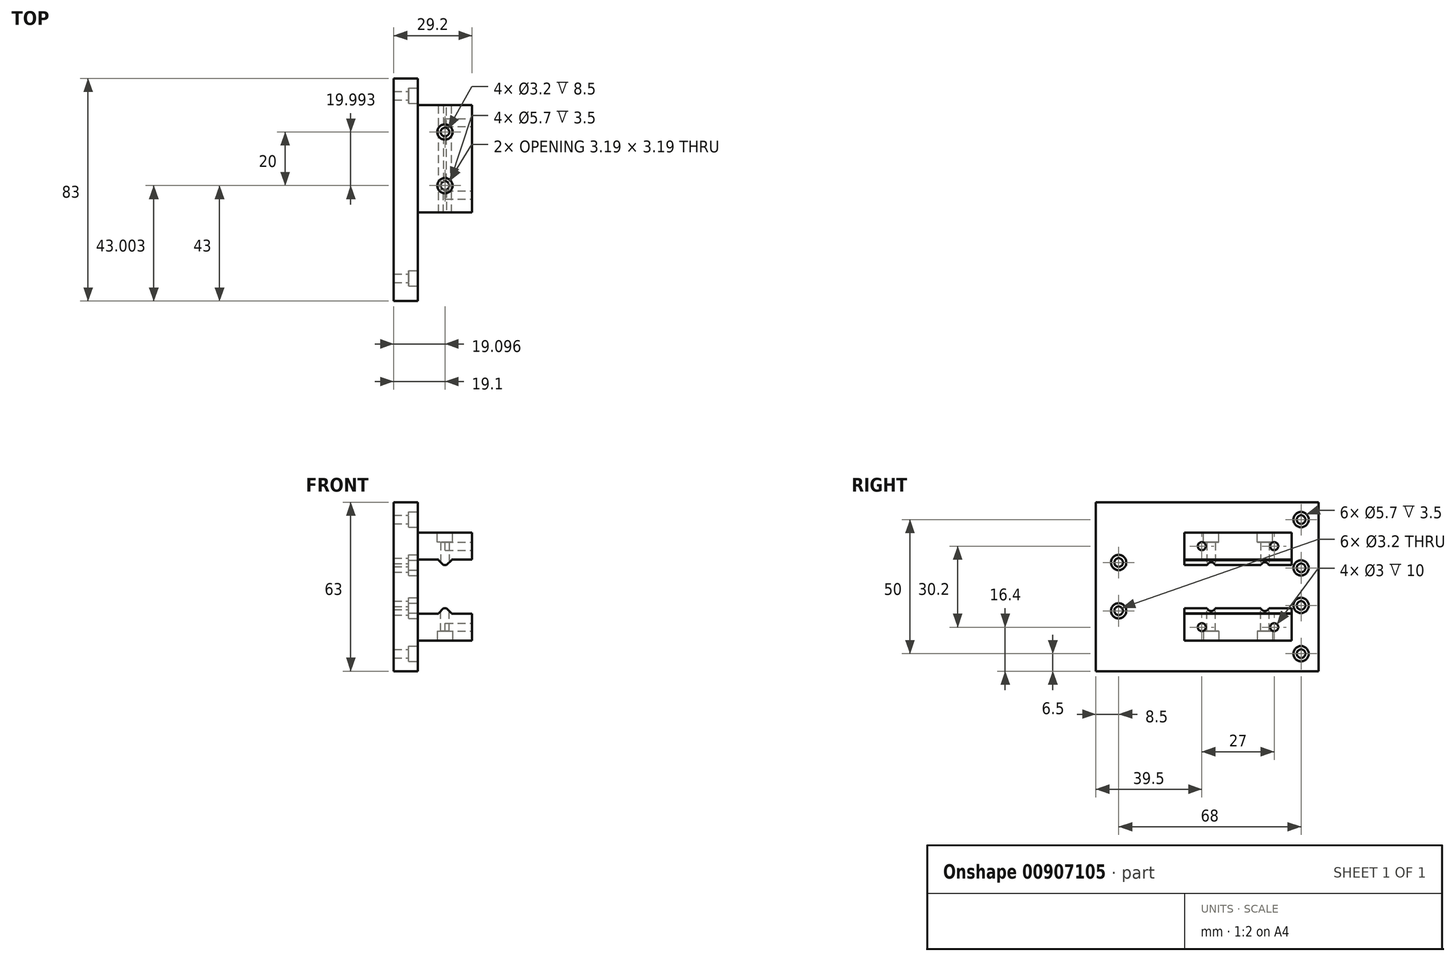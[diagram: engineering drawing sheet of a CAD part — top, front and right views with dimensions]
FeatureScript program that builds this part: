
annotation { "Feature Type Name" : "Feature", "Feature Type Description" : "" }
export const myFeature = defineFeature(function(context is Context, id is Id, definition is map)
    precondition{}
    {
        {
            assignVariable(context, id + "F0", {"name" : "headdepth", "anyValue" : 3.5 * mm});
        }
        {
            var Q0;
            Q0=qCreatedBy(makeId("Top.planeOp"),FACE);
            var sketch = newSketch(context, id + "F1", { "sketchPlane" : qUnion([Q0])});
            skLineSegment(sketch, "E0.bottom", {"start": v(0, 0) * mm, "end": v(9, 0) * mm});
            skLineSegment(sketch, "E0.top", {"start": v(0, 83) * mm, "end": v(9, 83) * mm});
            skLineSegment(sketch, "E0.left", {"start": v(0, 0) * mm, "end": v(0, 83) * mm});
            skLineSegment(sketch, "E0.right", {"start": v(9, 0) * mm, "end": v(9, 83) * mm});
            skSolve(sketch);
        }
        {
            var Q0;
            Q0=qSketchRegion(id+"F1",true);
            var Q1;
            Q1=makeQuery(id+"F1.imprint","IMPRINT",FACE,{"disambiguationData":[TD([[makeQuery(id+"F1.imprint","IMPRINT",EDGE,{"derivedFrom":sQuery(id+"F1.wireOp",EDGE,"E0.bottom")}),1.0]])]});
            extrude(context, id + "F2", {"entities" : qUnion([Q0, Q1]), "depth" : 63 * mm, "offsetDistance" : 25 * mm});
        }
        {
            var Q0;
            Q0=makeQuery(id+"F2.opExtrude","SWEPT_FACE",FACE,{"disambiguationData":[OSD([sQuery(id+"F1.wireOp",EDGE,"E0.right")])]});
            var sketch = newSketch(context, id + "F3", { "sketchPlane" : qUnion([Q0])});
            skLineSegment(sketch, "E1", {"start": v(83, 6.5) * mm, "end": v(0, 6.5) * mm, "construction": true});
            skLineSegment(sketch, "E2", {"start": v(0, 24.5) * mm, "end": v(83, 24.5) * mm, "construction": true});
            skLineSegment(sketch, "E3", {"start": v(83, 38.5) * mm, "end": v(0, 38.5) * mm, "construction": true});
            skLineSegment(sketch, "E4", {"start": v(0, 56.5) * mm, "end": v(83, 56.5) * mm, "construction": true});
            skLineSegment(sketch, "E5", {"start": v(76.5, 63) * mm, "end": v(76.5, 0) * mm, "construction": true});
            skLineSegment(sketch, "E6", {"start": v(8.5, 63) * mm, "end": v(8.5, 0) * mm, "construction": true});
            skLineSegment(sketch, "E7", {"start": v(0, 22.5) * mm, "end": v(8.5, 22.5) * mm, "construction": true});
            skLineSegment(sketch, "E8", {"start": v(0, 40.5) * mm, "end": v(8.5, 40.5) * mm, "construction": true});
            skCircle(sketch, "E9", {"center": v(8.5, 40.5) * mm, "radius": 2.85 * mm});
            skCircle(sketch, "E10", {"center": v(8.5, 22.5) * mm, "radius": 2.85 * mm});
            skCircle(sketch, "E11", {"center": v(76.5, 56.5) * mm, "radius": 2.85 * mm});
            skCircle(sketch, "E12", {"center": v(76.5, 38.5) * mm, "radius": 2.85 * mm});
            skCircle(sketch, "E13", {"center": v(76.5, 24.5) * mm, "radius": 2.85 * mm});
            skCircle(sketch, "E14", {"center": v(76.5, 6.5) * mm, "radius": 2.85 * mm});
            skSolve(sketch);
        }
        {
            var Q0;
            Q0=qSketchRegion(id+"F3",true);
            var Q1;
            Q1=makeQuery(id+"F3.imprint","IMPRINT",FACE,{"disambiguationData":[TD([[makeQuery(id+"F3.imprint","IMPRINT",EDGE,{"derivedFrom":sQuery(id+"F3.wireOp",EDGE,"E9")}),1.0]])]});
            extrude(context, id + "F4", {"entities" : qUnion([Q0, Q1]), "operationType" : NewBodyOperationType.REMOVE, "oppositeDirection" : true, "depth" : getVariable(context, 'headdepth'), "offsetDistance" : 25 * mm});
        }
        {
            var Q0;
            Q0=makeQuery(id+"F3.imprint","IMPRINT",FACE,{"disambiguationData":[TD([[makeQuery(id+"F3.imprint","IMPRINT",EDGE,{"derivedFrom":sQuery(id+"F3.wireOp",EDGE,"E9")}),1.0]])]});
            var sketch = newSketch(context, id + "F5", { "sketchPlane" : qUnion([Q0])});
            skCircle(sketch, "E15", {"center": v(8.5, 40.5) * mm, "radius": 1.6 * mm});
            skCircle(sketch, "E16", {"center": v(8.5, 22.5) * mm, "radius": 1.6 * mm});
            skCircle(sketch, "E17", {"center": v(76.5, 24.5) * mm, "radius": 1.6 * mm});
            skCircle(sketch, "E18", {"center": v(76.5, 38.5) * mm, "radius": 1.6 * mm});
            skCircle(sketch, "E19", {"center": v(76.5, 56.5) * mm, "radius": 1.6 * mm});
            skCircle(sketch, "E20", {"center": v(76.5, 6.5) * mm, "radius": 1.6 * mm});
            skSolve(sketch);
        }
        {
            var Q0;
            Q0=qSketchRegion(id+"F5",true);
            extrude(context, id + "F6", {"entities" : qUnion([Q0]), "operationType" : NewBodyOperationType.REMOVE, "oppositeDirection" : true, "depth" : 25 * mm, "offsetDistance" : 25 * mm});
        }
        {
            var Q0;
            Q0=makeQuery(id+"F2.opExtrude","SWEPT_FACE",FACE,{"disambiguationData":[OSD([sQuery(id+"F1.wireOp",EDGE,"E0.right")])]});
            var sketch = newSketch(context, id + "F7", { "sketchPlane" : qUnion([Q0])});
            skLineSegment(sketch, "E21", {"start": v(83, 31.5) * mm, "end": v(0, 31.5) * mm, "construction": true});
            skLineSegment(sketch, "E22.bottom", {"start": v(73, 41.6) * mm, "end": v(33, 41.6) * mm});
            skLineSegment(sketch, "E22.top", {"start": v(73, 51.6) * mm, "end": v(33, 51.6) * mm});
            skLineSegment(sketch, "E22.left", {"start": v(73, 41.6) * mm, "end": v(73, 51.6) * mm});
            skLineSegment(sketch, "E22.right", {"start": v(33, 41.6) * mm, "end": v(33, 51.6) * mm});
            skLineSegment(sketch, "E23.MirrorCS", {"start": v(73, 21.4) * mm, "end": v(73, 11.4) * mm});
            skLineSegment(sketch, "E24.MirrorCS", {"start": v(73, 21.4) * mm, "end": v(33, 21.4) * mm});
            skLineSegment(sketch, "E25.MirrorCS", {"start": v(73, 11.4) * mm, "end": v(33, 11.4) * mm});
            skLineSegment(sketch, "E26.MirrorCS", {"start": v(33, 21.4) * mm, "end": v(33, 11.4) * mm});
            skSolve(sketch);
        }
        {
            var Q0;
            Q0=makeQuery(id+"F7.imprint","IMPRINT",FACE,{"disambiguationData":[TD([[makeQuery(id+"F7.imprint","IMPRINT",EDGE,{"derivedFrom":sQuery(id+"F7.wireOp",EDGE,"E23.MirrorCS")}),-1.0]])]});
            var Q1;
            Q1=makeQuery(id+"F7.imprint","IMPRINT",FACE,{"disambiguationData":[TD([[makeQuery(id+"F7.imprint","IMPRINT",EDGE,{"derivedFrom":sQuery(id+"F7.wireOp",EDGE,"E22.bottom")}),-1.0]])]});
            extrude(context, id + "F8", {"entities" : qUnion([Q0, Q1]), "operationType" : NewBodyOperationType.ADD, "depth" : 20.2 * mm, "offsetDistance" : 25 * mm});
        }
        {
            var Q0;
            Q0=makeQuery(id+"F8.opExtrude","SWEPT_FACE",FACE,{"disambiguationData":[OSD([sQuery(id+"F7.wireOp",EDGE,"E22.bottom")])]});
            var sketch = newSketch(context, id + "F9", { "sketchPlane" : qUnion([Q0])});
            skLineSegment(sketch, "E27", {"start": v(19.1, -33) * mm, "end": v(19.1, -73) * mm, "construction": true});
            skLineSegment(sketch, "E28.bottom", {"start": v(21.5, -33) * mm, "end": v(16.7, -33) * mm});
            skLineSegment(sketch, "E28.top", {"start": v(21.5, -73) * mm, "end": v(16.7, -73) * mm});
            skLineSegment(sketch, "E28.left", {"start": v(21.5, -33) * mm, "end": v(21.5, -73) * mm});
            skLineSegment(sketch, "E28.right", {"start": v(16.7, -33) * mm, "end": v(16.7, -73) * mm});
            skSolve(sketch);
        }
        {
            var Q0;
            Q0=qSketchRegion(id+"F9",true);
            extrude(context, id + "F10", {"entities" : qUnion([Q0]), "operationType" : NewBodyOperationType.ADD, "depth" : 2 * mm, "offsetDistance" : 25 * mm});
        }
        {
            var Q0;
            Q0=makeQuery(id+"F10.opExtrude","CAP_EDGE",EDGE,{"disambiguationData":[OSD([sQuery(id+"F9.wireOp",EDGE,"E28.left")])],"isStart":false});
            var Q1;
            Q1=makeQuery(id+"F10.opExtrude","CAP_EDGE",EDGE,{"disambiguationData":[OSD([sQuery(id+"F9.wireOp",EDGE,"E28.right")])],"isStart":false});
            chamfer(context, id + "F11", {"entities" : qUnion([Q0, Q1]), "width" : 1.8 * mm, "tangentPropagation" : true});
        }
        {
            var Q0;
            Q0=makeQuery(id+"F10.opExtrude","CAP_FACE",FACE,{"disambiguationData":[OSD([sQuery(id+"F9.wireOp",EDGE,"E28.bottom"),sQuery(id+"F9.wireOp",EDGE,"E28.top"),sQuery(id+"F9.wireOp",EDGE,"E28.left"),sQuery(id+"F9.wireOp",EDGE,"E28.right")])],"isStart":false});
            var sketch = newSketch(context, id + "F12", { "sketchPlane" : qUnion([Q0])});
            skLineSegment(sketch, "E29", {"start": v(19.1, -33) * mm, "end": v(19.1, -73) * mm, "construction": true});
            skCircle(sketch, "E30", {"center": v(19.1, -43) * mm, "radius": 1.6 * mm});
            skCircle(sketch, "E31", {"center": v(19.1, -63) * mm, "radius": 1.6 * mm});
            skSolve(sketch);
        }
        {
            var Q0;
            Q0=qSketchRegion(id+"F12",true);
            extrude(context, id + "F13", {"entities" : qUnion([Q0]), "operationType" : NewBodyOperationType.REMOVE, "oppositeDirection" : true, "depth" : 25 * mm, "offsetDistance" : 25 * mm});
        }
        {
            var Q0;
            Q0=makeQuery(id+"F8.opExtrude","SWEPT_FACE",FACE,{"disambiguationData":[OSD([sQuery(id+"F7.wireOp",EDGE,"E24.MirrorCS")])]});
            var sketch = newSketch(context, id + "F14", { "sketchPlane" : qUnion([Q0])});
            skLineSegment(sketch, "E32", {"start": v(19.1, 73) * mm, "end": v(19.1, 33) * mm, "construction": true});
            skLineSegment(sketch, "E33.bottom", {"start": v(21.5, 33) * mm, "end": v(16.7, 33) * mm});
            skLineSegment(sketch, "E33.top", {"start": v(21.5, 73) * mm, "end": v(16.7, 73) * mm});
            skLineSegment(sketch, "E33.left", {"start": v(21.5, 33) * mm, "end": v(21.5, 73) * mm});
            skLineSegment(sketch, "E33.right", {"start": v(16.7, 33) * mm, "end": v(16.7, 73) * mm});
            skSolve(sketch);
        }
        {
            var Q0;
            Q0=qSketchRegion(id+"F14",true);
            extrude(context, id + "F15", {"entities" : qUnion([Q0]), "operationType" : NewBodyOperationType.ADD, "depth" : 2 * mm, "offsetDistance" : 25 * mm});
        }
        {
            var Q0;
            Q0=makeQuery(id+"F15.opExtrude","CAP_EDGE",EDGE,{"disambiguationData":[OSD([sQuery(id+"F14.wireOp",EDGE,"E33.left")])],"isStart":false});
            var Q1;
            Q1=makeQuery(id+"F15.opExtrude","CAP_EDGE",EDGE,{"disambiguationData":[OSD([sQuery(id+"F14.wireOp",EDGE,"E33.right")])],"isStart":false});
            chamfer(context, id + "F16", {"entities" : qUnion([Q0, Q1]), "width" : 1.8 * mm, "tangentPropagation" : true});
        }
        {
            var Q0;
            Q0=makeQuery(id+"F15.opExtrude","CAP_FACE",FACE,{"disambiguationData":[OSD([sQuery(id+"F14.wireOp",EDGE,"E33.bottom"),sQuery(id+"F14.wireOp",EDGE,"E33.top"),sQuery(id+"F14.wireOp",EDGE,"E33.left"),sQuery(id+"F14.wireOp",EDGE,"E33.right")])],"isStart":false});
            var sketch = newSketch(context, id + "F17", { "sketchPlane" : qUnion([Q0])});
            skLineSegment(sketch, "E34", {"start": v(19.1, 73) * mm, "end": v(19.1, 33) * mm, "construction": true});
            skCircle(sketch, "E35", {"center": v(19.1, 43) * mm, "radius": 1.6 * mm});
            skCircle(sketch, "E36", {"center": v(19.1, 63) * mm, "radius": 1.6 * mm});
            skSolve(sketch);
        }
        {
            var Q0;
            Q0=qSketchRegion(id+"F17",true);
            extrude(context, id + "F18", {"entities" : qUnion([Q0]), "operationType" : NewBodyOperationType.REMOVE, "oppositeDirection" : true, "depth" : 25 * mm, "offsetDistance" : 25 * mm});
        }
        {
            var Q0;
            Q0=makeQuery(id+"F8.opExtrude","SWEPT_FACE",FACE,{"disambiguationData":[OSD([sQuery(id+"F7.wireOp",EDGE,"E25.MirrorCS")])]});
            var sketch = newSketch(context, id + "F19", { "sketchPlane" : qUnion([Q0])});
            skCircle(sketch, "E37", {"center": v(19.1, -43) * mm, "radius": 2.85 * mm});
            skCircle(sketch, "E38", {"center": v(19.1, -63) * mm, "radius": 2.85 * mm});
            skSolve(sketch);
        }
        {
            var Q0;
            Q0=qSketchRegion(id+"F19",true);
            extrude(context, id + "F20", {"entities" : qUnion([Q0]), "operationType" : NewBodyOperationType.REMOVE, "oppositeDirection" : true, "depth" : 3.5 * mm, "offsetDistance" : 25 * mm});
        }
        {
            var Q0;
            Q0=makeQuery(id+"F8.opExtrude","SWEPT_FACE",FACE,{"disambiguationData":[OSD([sQuery(id+"F7.wireOp",EDGE,"E22.top")])]});
            var sketch = newSketch(context, id + "F21", { "sketchPlane" : qUnion([Q0])});
            skCircle(sketch, "E39", {"center": v(19.1, 63) * mm, "radius": 2.85 * mm});
            skCircle(sketch, "E40", {"center": v(19.1, 43) * mm, "radius": 2.85 * mm});
            skSolve(sketch);
        }
        {
            var Q0;
            Q0=qSketchRegion(id+"F21",true);
            extrude(context, id + "F22", {"entities" : qUnion([Q0]), "operationType" : NewBodyOperationType.REMOVE, "oppositeDirection" : true, "depth" : 3.5 * mm, "offsetDistance" : 25 * mm});
        }
        {
            var Q0;
            Q0=makeQuery(id+"F8.opExtrude","CAP_FACE",FACE,{"disambiguationData":[OSD([sQuery(id+"F7.wireOp",EDGE,"E23.MirrorCS"),sQuery(id+"F7.wireOp",EDGE,"E24.MirrorCS"),sQuery(id+"F7.wireOp",EDGE,"E25.MirrorCS"),sQuery(id+"F7.wireOp",EDGE,"E26.MirrorCS")])],"isStart":false});
            var sketch = newSketch(context, id + "F23", { "sketchPlane" : qUnion([Q0])});
            skLineSegment(sketch, "E41", {"start": v(73, 16.4) * mm, "end": v(33, 16.4) * mm, "construction": true});
            skLineSegment(sketch, "E42", {"start": v(66.5, 11.4) * mm, "end": v(66.5, 21.4) * mm, "construction": true});
            skLineSegment(sketch, "E43", {"start": v(53, 11.4) * mm, "end": v(53, 21.4) * mm, "construction": true});
            skLineSegment(sketch, "E44", {"start": v(39.5, 11.4) * mm, "end": v(39.5, 21.4) * mm, "construction": true});
            skCircle(sketch, "E45", {"center": v(66.5, 16.4) * mm, "radius": 1.5 * mm});
            skCircle(sketch, "E46", {"center": v(39.5, 16.4) * mm, "radius": 1.5 * mm});
            skCircle(sketch, "E47.MirrorC", {"center": v(39.5, 46.6) * mm, "radius": 1.5 * mm});
            skCircle(sketch, "E48.MirrorC", {"center": v(66.5, 46.6) * mm, "radius": 1.5 * mm});
            skSolve(sketch);
        }
        {
            var Q0;
            Q0=qSketchRegion(id+"F23",true);
            extrude(context, id + "F24", {"entities" : qUnion([Q0]), "operationType" : NewBodyOperationType.REMOVE, "oppositeDirection" : true, "depth" : 10 * mm, "offsetDistance" : 25 * mm});
        }
    });
